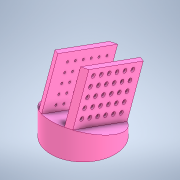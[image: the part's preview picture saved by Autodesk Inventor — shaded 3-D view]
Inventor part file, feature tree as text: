
AUTODESK INVENTOR PART (.ipt)
format: ipt  version: 2022.2 (Build 262287000, 287)  size: 360,960 bytes
history: native  units: mm
features: sketch x6, extrude x3, hole x3, mirror x1
ambient origin geometry x8: Origin, YZ Plane, XZ Plane, XY Plane, X Axis, Y Axis, Z Axis, Center Point
bodies: Solid5 (feature_tree)
feature tree (13):
  extrude  "Extrusion34"  Depth=60.0mm TaperAngle=0.0deg
  extrude  "Extrusion35"  Depth=10.0mm
  extrude  "Extrusion38"  Depth=10.0mm
  mirror  "Mirror6"
  hole  "Hole10"  [1 undecoded]
  hole  "Hole11"  [1 undecoded]
  hole  "Hole12"  [1 undecoded]
  sketch  "Sketch85"  dims[d360=114.3mm d361=60.0mm d362=0.0mm]
  sketch  "Sketch86"  dims[d363=10.0mm d364=3.490659mm]
  sketch  "Sketch90"  dims[d365=0.0mm d366=0.0mm d378=10.0mm]
  sketch  "Sketch91"  dims[d379=20.32mm d380=84.1375mm d381=0.0mm]
  sketch  "Sketch92"  dims[d382=10.0mm d383=10.0mm]
  sketch  "Sketch93"  dims[d384=60.0mm d386=15.0mm d387=50.0mm d389=15.0mm d392=3.797mm d393=6.0mm d394=7.087mm d395=3.048mm d396=14.3117mm d397=8.0mm d398=0.0mm d399=14.0mm d400=12.0mm d401=60.0mm d403=15.0mm d404=50.0mm d406=15.0mm d409=3.797mm d410=6.0mm d411=7.087mm d412=2.0mm d413=14.3117mm d414=8.0mm d415=0.0mm d416=47.625mm d417=120.0mm d419=360.0deg d421=6.3754mm d422=6.0mm d423=6.985mm d424=5.76834mm d425=14.3117mm d426=10.0mm d427=0.0mm d64=1.0mm d65=1.0mm d66=1.0mm d67=0.15mm d68=0.25mm d69=0.375mm d70=14.3117mm d71=0.75mm d72=20.594885mm d73=0.0625mm d74=0.75mm d75=0.375mm]
note: 3 required parameter values undecoded (feature->parameter linkage not recoverable at this tier; creation-order binding heuristic only, values carry confidence <= 0.55)
